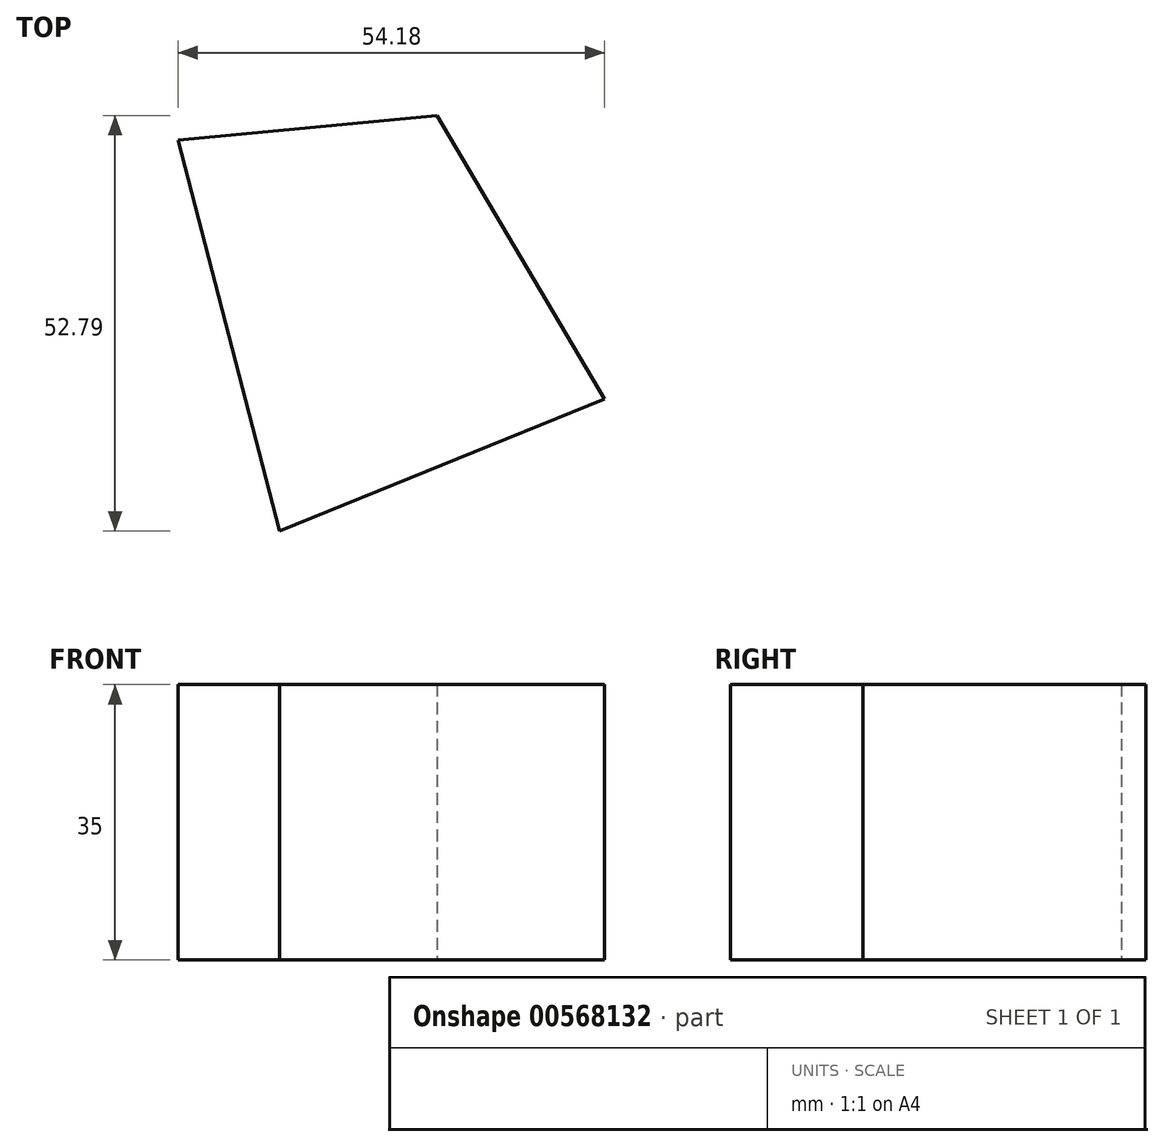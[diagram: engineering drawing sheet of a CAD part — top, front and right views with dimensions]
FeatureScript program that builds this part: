
annotation { "Feature Type Name" : "Feature", "Feature Type Description" : "" }
export const myFeature = defineFeature(function(context is Context, id is Id, definition is map)
    precondition{}
    {
        {
            var Q0;
            Q0=qCreatedBy(makeId("Top.planeOp"),FACE);
            var sketch = newSketch(context, id + "F0", { "sketchPlane" : qUnion([Q0])});
            skLineSegment(sketch, "E0", {"start": v(-32.87, 32.86) * mm, "end": v(-19.98, -16.8) * mm});
            skLineSegment(sketch, "E1", {"start": v(-19.98, -16.8) * mm, "end": v(21.3, 0) * mm});
            skLineSegment(sketch, "E2", {"start": v(21.3, 0) * mm, "end": v(0, 36) * mm});
            skLineSegment(sketch, "E3", {"start": v(0, 36) * mm, "end": v(-32.87, 32.86) * mm});
            skSolve(sketch);
        }
        {
            var Q0;
            Q0 = qSketchRegion(id + "F0", true);
            extrude(context, id + "F1", {"entities" : qUnion([Q0]), "depth" : 35 * mm, "offsetDistance" : 25 * mm});
        }
    });
